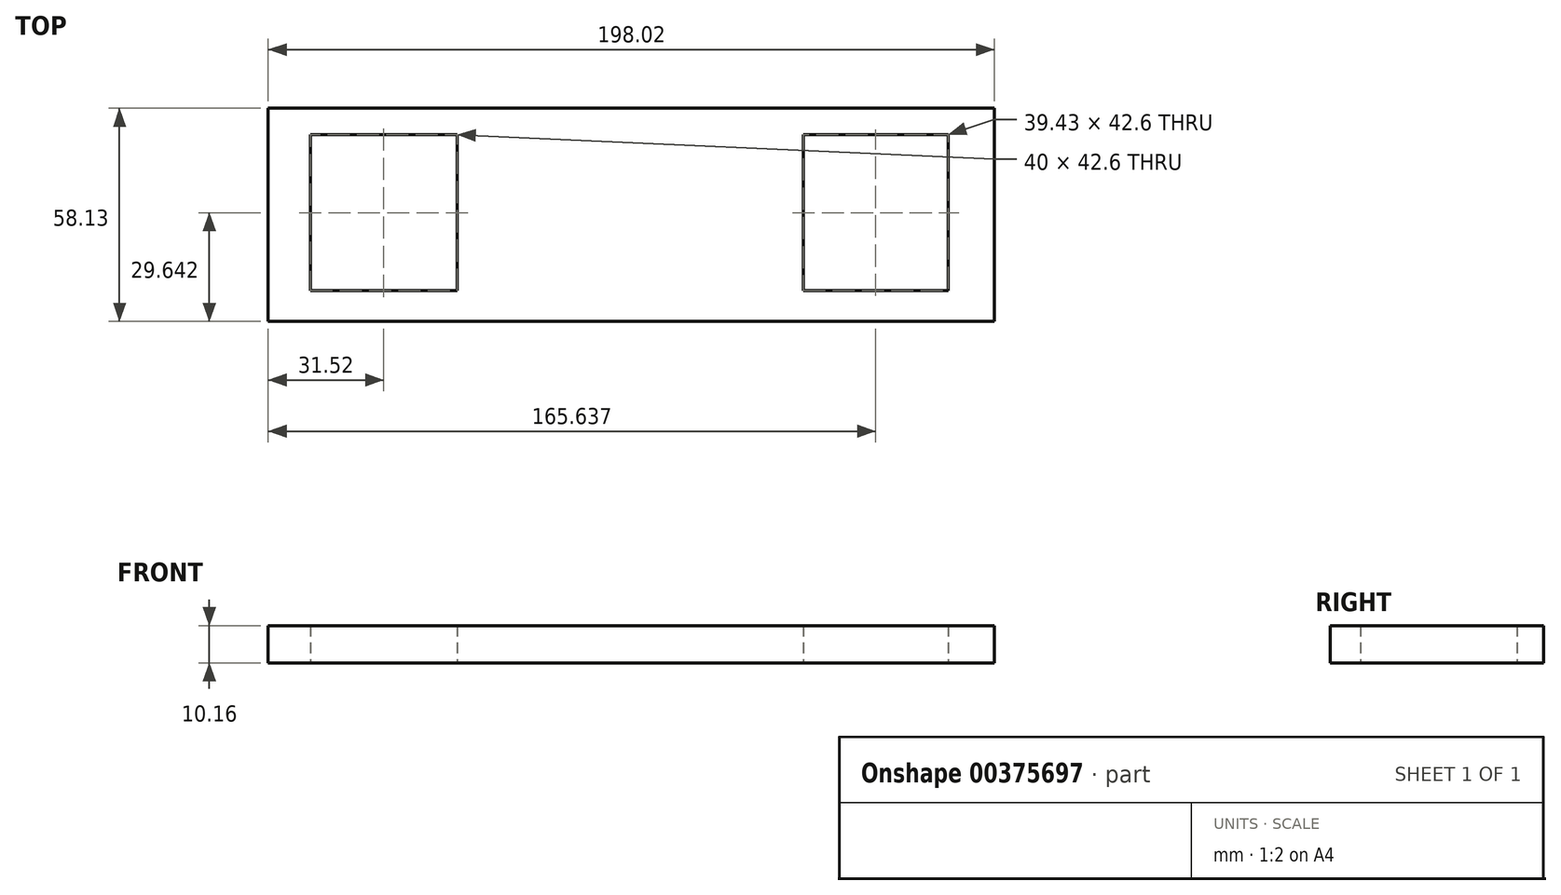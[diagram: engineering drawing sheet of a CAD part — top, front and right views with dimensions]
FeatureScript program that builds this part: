
annotation { "Feature Type Name" : "Feature", "Feature Type Description" : "" }
export const myFeature = defineFeature(function(context is Context, id is Id, definition is map)
    precondition{}
    {
        {
            var Q0;
            Q0=qCreatedBy(makeId("Top.planeOp"),FACE);
            var sketch = newSketch(context, id + "F0", { "sketchPlane" : qUnion([Q0])});
            skLineSegment(sketch, "E0", {"start": v(-99, 34.82) * mm, "end": v(-99, -23.31) * mm});
            skLineSegment(sketch, "E1", {"start": v(-99, -23.31) * mm, "end": v(99, -23.31) * mm});
            skLineSegment(sketch, "E2", {"start": v(99, -23.31) * mm, "end": v(99, 34.82) * mm});
            skLineSegment(sketch, "E3", {"start": v(99, 34.82) * mm, "end": v(-99, 34.82) * mm});
            skLineSegment(sketch, "E4", {"start": v(-87.5, 27.63) * mm, "end": v(-87.5, -14.97) * mm});
            skLineSegment(sketch, "E5", {"start": v(-87.5, -14.97) * mm, "end": v(-47.49, -14.97) * mm});
            skLineSegment(sketch, "E6", {"start": v(-47.49, -14.97) * mm, "end": v(-47.49, 27.63) * mm});
            skLineSegment(sketch, "E7", {"start": v(-47.49, 27.63) * mm, "end": v(-87.5, 27.63) * mm});
            skLineSegment(sketch, "E8", {"start": v(86.34, 27.63) * mm, "end": v(86.34, -14.97) * mm});
            skPoint(sketch, "E8.startSnap0", {"position": v(-67.5, 27.63) * mm});
            skLineSegment(sketch, "E9", {"start": v(86.34, -14.97) * mm, "end": v(46.91, -14.97) * mm});
            skLineSegment(sketch, "E10", {"start": v(46.91, -14.97) * mm, "end": v(46.91, 27.63) * mm});
            skLineSegment(sketch, "E11", {"start": v(46.91, 27.63) * mm, "end": v(86.34, 27.63) * mm});
            skSolve(sketch);
        }
        {
            var Q0;
            Q0 = qSketchRegion(id + "F0", true);
            extrude(context, id + "F1", {"entities" : qUnion([Q0]), "depth" : 10.16 * mm});
        }
    });
